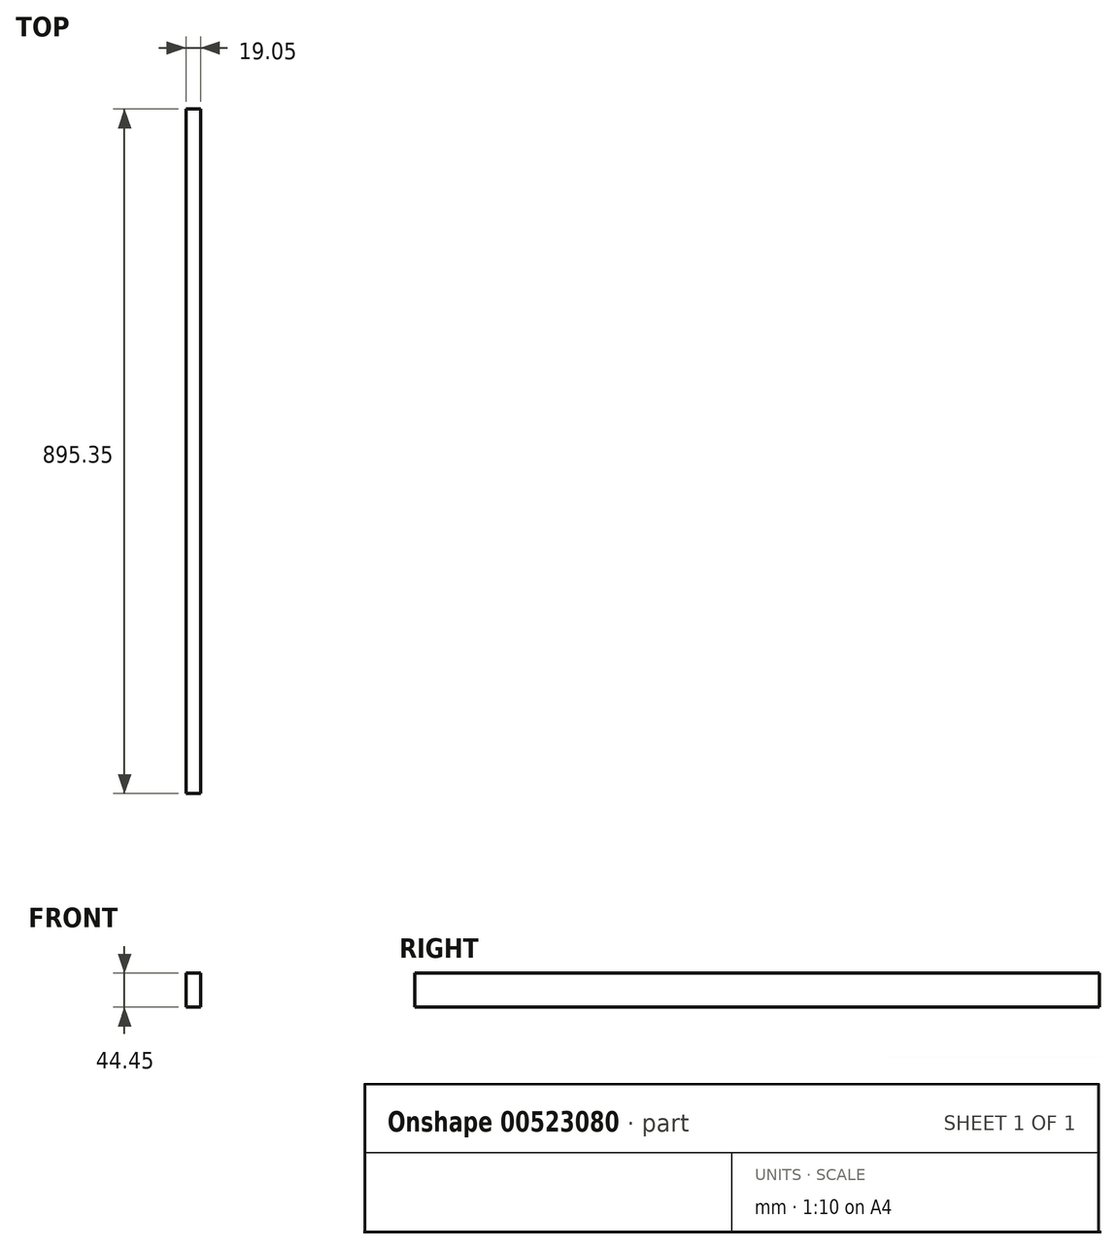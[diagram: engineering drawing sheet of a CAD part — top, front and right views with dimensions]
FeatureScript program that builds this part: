
annotation { "Feature Type Name" : "Feature", "Feature Type Description" : "" }
export const myFeature = defineFeature(function(context is Context, id is Id, definition is map)
    precondition{}
    {
        {
            var Q0;
            Q0=qCreatedBy(makeId("Front.planeOp"),FACE);
            var sketch = newSketch(context, id + "F0", { "sketchPlane" : qUnion([Q0])});
            skLineSegment(sketch, "E0.bottom", {"start": v(0, 0) * mm, "end": v(19.05, 0) * mm});
            skLineSegment(sketch, "E0.top", {"start": v(0, 44.45) * mm, "end": v(19.05, 44.45) * mm});
            skLineSegment(sketch, "E0.left", {"start": v(0, 0) * mm, "end": v(0, 44.45) * mm});
            skLineSegment(sketch, "E0.right", {"start": v(19.05, 0) * mm, "end": v(19.05, 44.45) * mm});
            skSolve(sketch);
        }
        {
            var Q0;
            Q0=qSketchRegion(id+"F0",true);
            extrude(context, id + "F1", {"entities" : qUnion([Q0]), "depth" : 895.35 * mm, "offsetDistance" : 25.4 * mm});
        }
    });
